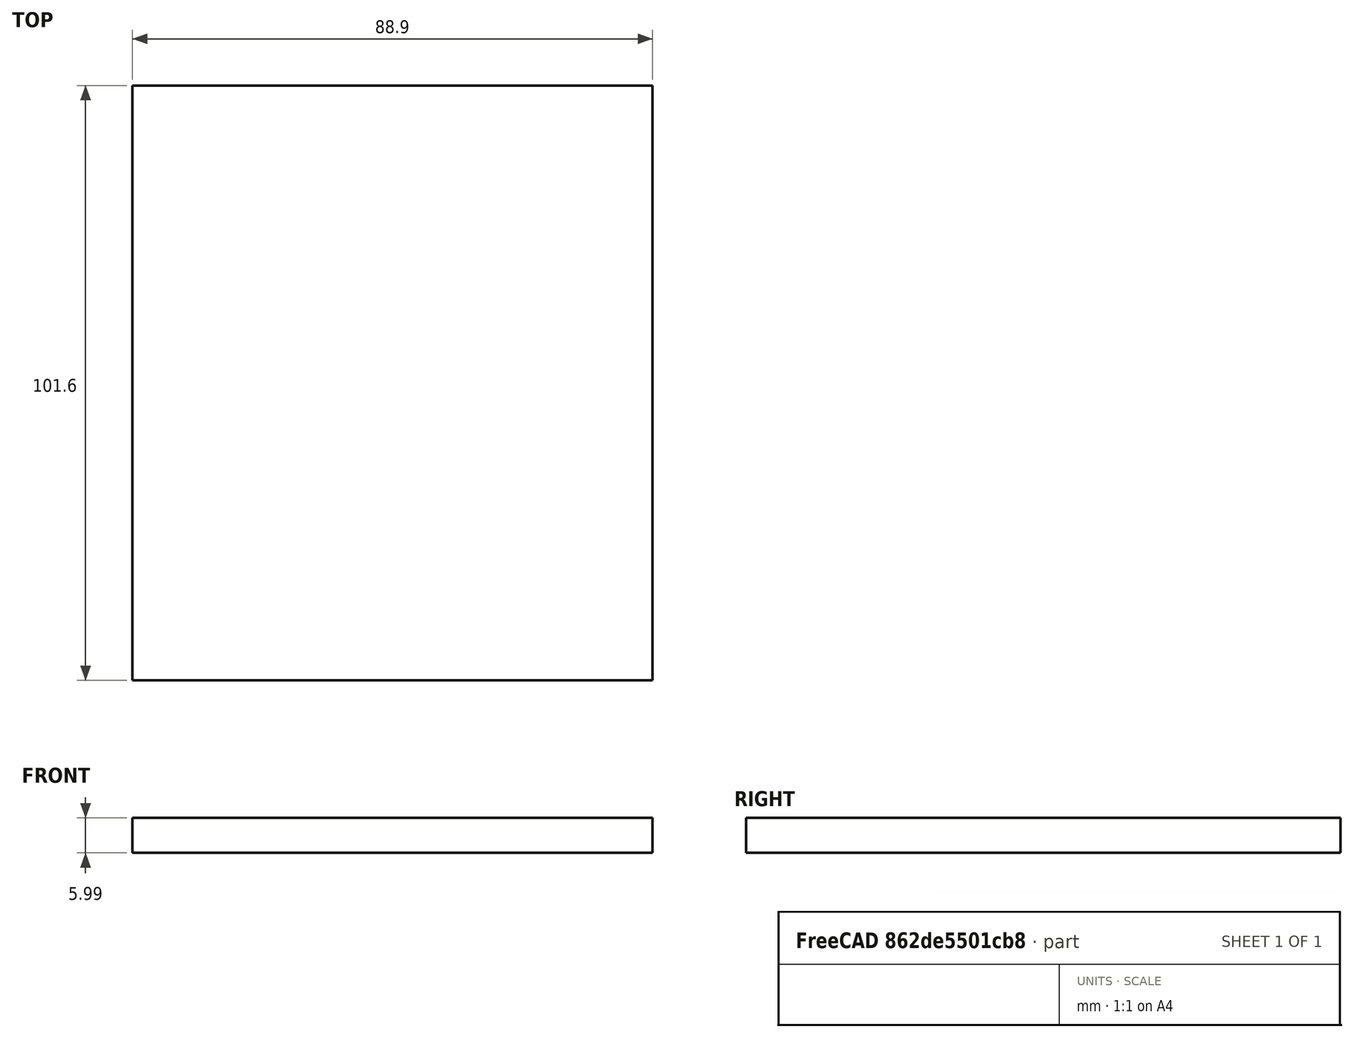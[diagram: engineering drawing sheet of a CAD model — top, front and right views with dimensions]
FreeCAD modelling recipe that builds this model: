
FCSTD DOCUMENT  (FreeCAD 0.19R24267 (Git))
Label: Inv1-P14
License: All rights reserved
LicenseURL: http://en.wikipedia.org/wiki/All_rights_reserved
objects: TechDraw::DrawViewDimension×3, TechDraw::DrawProjGroupItem×2, TechDraw::DrawHatch×2, TechDraw::DrawViewAnnotation×2, Sketcher::SketchObject×1, Part::Extrusion×1, TechDraw::DrawSVGTemplate×1, TechDraw::DrawProjGroup×1, TechDraw::DrawPage×1
note: 2 computed .brp shape members not serialized (recipe doc carries the construction recipe); baked Part::Feature solids carry a one-line shape summary decoded from their .brp

FEATURE [Sketcher::SketchObject] Sketch
  FullyConstrained = false
  sketch-geometry (4):
    g0: LineSegment StartX=-49.1218 StartY=33.4156 StartZ=0 EndX=39.7782 EndY=33.4156 EndZ=0
    g1: LineSegment StartX=39.7782 StartY=33.4156 StartZ=0 EndX=39.7782 EndY=-68.1844 EndZ=0
    g2: LineSegment StartX=39.7782 StartY=-68.1844 StartZ=0 EndX=-49.1218 EndY=-68.1844 EndZ=0
    g3: LineSegment StartX=-49.1218 StartY=-68.1844 StartZ=0 EndX=-49.1218 EndY=33.4156 EndZ=0
  constraints (10):
    c: Coincident(g0,g1)
    c: Coincident(g1,g2)
    c: Coincident(g2,g3)
    c: Coincident(g3,g0)
    c: Horizontal(g0)
    c: Horizontal(g2)
    c: Vertical(g1)
    c: Vertical(g3)
    c: DistanceX(g0,g0) = 88.9
    c: DistanceY(g3,g3) = 101.6
FEATURE [Part::Extrusion] Extrude
  Base = -> Sketch
  Dir = (0,0,1)
  DirMode = 2
  FaceMakerClass = Part::FaceMakerBullseye
  LengthFwd = 5.9944
  LengthRev = 0
  Solid = true
  Symmetric = false
FEATURE [TechDraw::DrawSVGTemplate] Template
  Height = 215.9
  Orientation = 1
  Width = 279.4
FEATURE [TechDraw::DrawProjGroupItem] ProjItem  label="Front"
  CoarseView = false
  Direction = (0,0,-1)
  Focus = 100
  HardHidden = false
  IsoCount = 0
  IsoHidden = false
  IsoVisible = false
  LockPosition = true
  Perspective = false
  Rotation = 0
  RotationVector = (1,0,0)
  Scale = 0.5
  ScaleType = 2
  SeamHidden = false
  SeamVisible = true
  SmoothHidden = false
  SmoothVisible = true
  Source = -> [Extrude]
  Type = 0
  X = 0
  XDirection = (1,0,0)
  Y = 0
FEATURE [TechDraw::DrawProjGroupItem] ProjItem001  label="Left"
  CoarseView = false
  Direction = (-1,0,-1e-16)
  Focus = 100
  HardHidden = false
  IsoCount = 0
  IsoHidden = false
  IsoVisible = false
  LockPosition = false
  Perspective = false
  Rotation = 0
  RotationVector = (1,0,0)
  Scale = 0.5
  ScaleType = 2
  SeamHidden = false
  SeamVisible = true
  SmoothHidden = false
  SmoothVisible = true
  Source = -> [Extrude]
  Type = 1
  X = 59.5032
  XDirection = (1e-16,0,-1)
  Y = 0
FEATURE [TechDraw::DrawProjGroup] ProjGroup
  Anchor = -> ProjItem
  AutoDistribute = true
  LockPosition = false
  ProjectionType = 0
  Rotation = 0
  Scale = 0.5
  ScaleType = 2
  Source = -> [Extrude]
  Views = -> [ProjItem,ProjItem001]
  X = 128.016
  Y = 109.159
  spacingX = 15.0114
  spacingY = 15.0114
FEATURE [TechDraw::DrawHatch] Hatch  label="HatchF0"
  HatchPattern = <path>
  Source = -> ProjItem [Face0]
FEATURE [TechDraw::DrawHatch] Hatch001  label="Hatch001F0"
  HatchPattern = <path>
  Source = -> ProjItem001 [Face0]
FEATURE [TechDraw::DrawViewAnnotation] Annotation
  Font = osifont
  LineSpace = 80
  LockPosition = false
  MaxWidth = -1
  Rotation = 0
  ScaleType = 0
  Text = Figure S1 (Inverted 1) | Panel 14 [lower door] | Quantity: 1
  TextSize = 5.0038
  TextStyle = 0
  X = 32.1499
  Y = 195.58
FEATURE [TechDraw::DrawViewAnnotation] Annotation002
  Font = osifont
  LineSpace = 80
  LockPosition = false
  MaxWidth = -1
  Rotation = 0
  ScaleType = 0
  Text = Units: Inches
  TextSize = 5.0038
  TextStyle = 0
  X = 259.08
  Y = 5.08
FEATURE [TechDraw::DrawViewDimension] Dimension
  Arbitrary = false
  ArbitraryTolerances = false
  EqualTolerance = true
  FormatSpec = %.3f
  FormatSpecOverTolerance = %+.3f
  FormatSpecUnderTolerance = %+.3f
  Inverted = false
  LockPosition = false
  MeasureType = 1
  OverTolerance = 0
  References2D = -> [ProjItem]
  Rotation = 0
  ScaleType = 0
  TheoreticalExact = false
  Type = 1
  UnderTolerance = 0
  X = -1.12261
  Y = -40.8358
FEATURE [TechDraw::DrawViewDimension] Dimension001
  Arbitrary = false
  ArbitraryTolerances = false
  EqualTolerance = true
  FormatSpec = %.3f
  FormatSpecOverTolerance = %+.3f
  FormatSpecUnderTolerance = %+.3f
  Inverted = false
  LockPosition = false
  MeasureType = 1
  OverTolerance = 0
  References2D = -> [ProjItem]
  Rotation = 0
  ScaleType = 0
  TheoreticalExact = false
  Type = 2
  UnderTolerance = 0
  X = 41.0286
  Y = 0
FEATURE [TechDraw::DrawViewDimension] Dimension002
  Arbitrary = false
  ArbitraryTolerances = false
  EqualTolerance = true
  FormatSpec = %.3f
  FormatSpecOverTolerance = %+.3f
  FormatSpecUnderTolerance = %+.3f
  Inverted = false
  LockPosition = false
  MeasureType = 1
  OverTolerance = 0
  References2D = -> [ProjItem001]
  Rotation = 0
  ScaleType = 0
  TheoreticalExact = false
  Type = 1
  UnderTolerance = 0
  X = 24.136
  Y = 16.6998
FEATURE [TechDraw::DrawPage] Page
  KeepUpdated = true
  NextBalloonIndex = 1
  ProjectionType = 0
  Template = -> Template
  Views = -> [ProjGroup,Annotation,Annotation002,Dimension,Dimension001,Dimension002]
note: 2 file-system paths scrubbed to <path> (originals preserved in the JSON sidecar)
